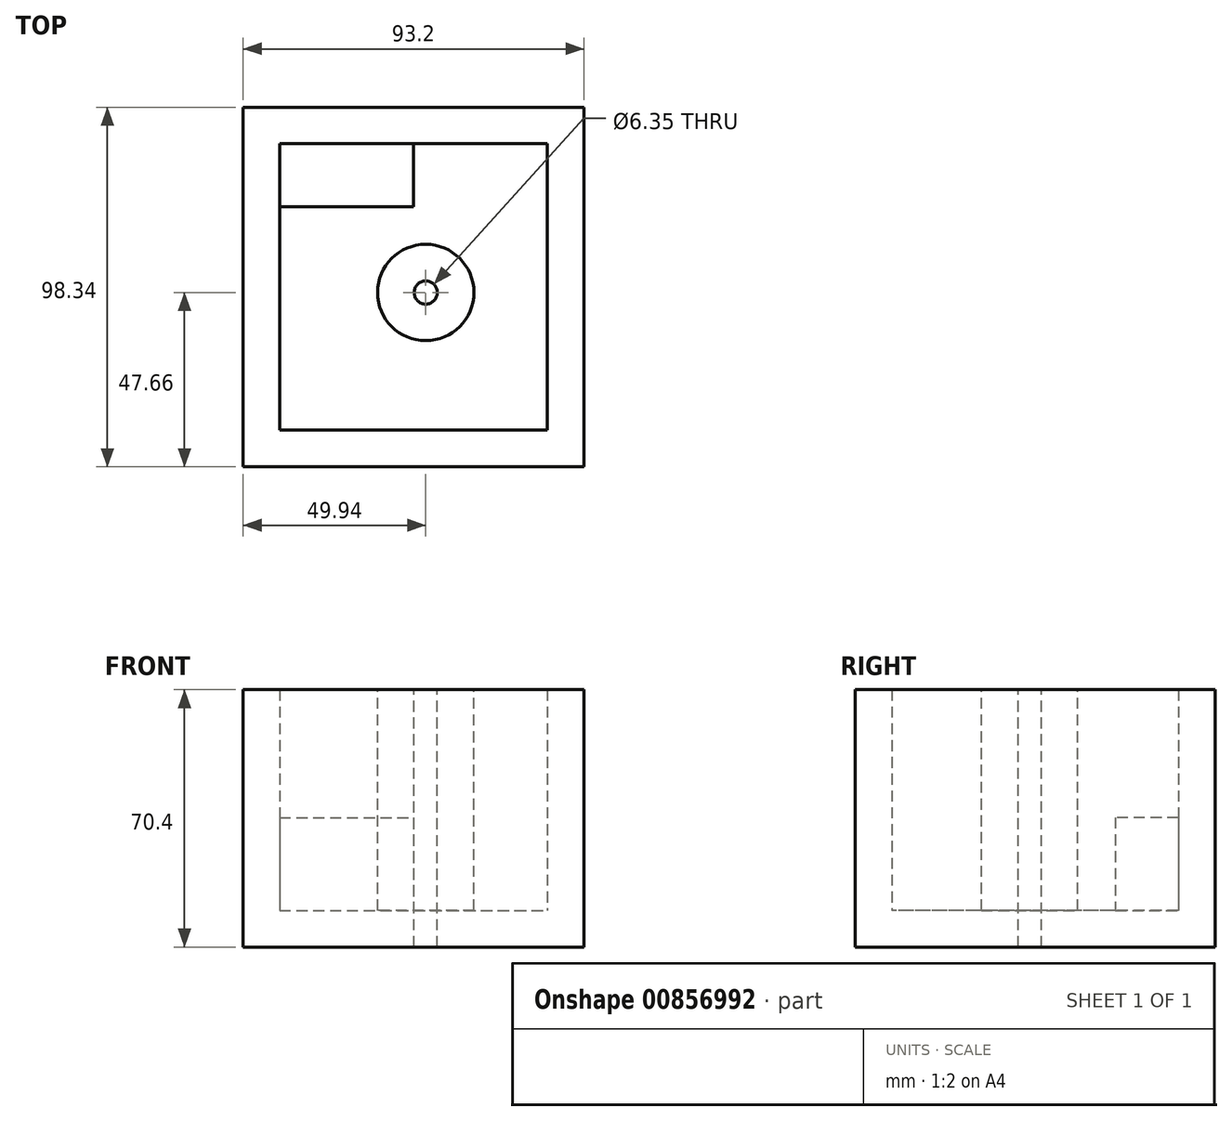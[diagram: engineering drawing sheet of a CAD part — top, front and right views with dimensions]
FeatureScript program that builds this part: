
annotation { "Feature Type Name" : "Feature", "Feature Type Description" : "" }
export const myFeature = defineFeature(function(context is Context, id is Id, definition is map)
    precondition{}
    {
        {
            var Q0;
            Q0=qCreatedBy(makeId("Top.planeOp"),FACE);
            var sketch = newSketch(context, id + "F0", { "sketchPlane" : qUnion([Q0])});
            skLineSegment(sketch, "E0.bottom", {"start": v(-49.94, 50.68) * mm, "end": v(43.26, 50.68) * mm});
            skLineSegment(sketch, "E0.top", {"start": v(-49.94, -47.66) * mm, "end": v(43.26, -47.66) * mm});
            skLineSegment(sketch, "E0.left", {"start": v(-49.94, 50.68) * mm, "end": v(-49.94, -47.66) * mm});
            skLineSegment(sketch, "E0.right", {"start": v(43.26, 50.68) * mm, "end": v(43.26, -47.66) * mm});
            skSolve(sketch);
        }
        {
            var Q0;
            Q0=makeQuery(id+"F0.imprint","IMPRINT",FACE,{"disambiguationData":[TD([[makeQuery(id+"F0.imprint","IMPRINT",EDGE,{"derivedFrom":sQuery(id+"F0.wireOp",EDGE,"E0.bottom")}),-1.0]])]});
            extrude(context, id + "F1", {"entities" : qUnion([Q0]), "depth" : 25.4 * mm, "offsetDistance" : 25.4 * mm});
        }
        {
            var Q0;
            Q0=makeQuery(id+"F1.opExtrude","CAP_FACE",FACE,{"disambiguationData":[OSD([sQuery(id+"F0.wireOp",EDGE,"E0.bottom"),sQuery(id+"F0.wireOp",EDGE,"E0.top"),sQuery(id+"F0.wireOp",EDGE,"E0.left"),sQuery(id+"F0.wireOp",EDGE,"E0.right")])],"isStart":false});
            extrude(context, id + "F2", {"entities" : qUnion([Q0]), "operationType" : NewBodyOperationType.ADD, "depth" : 45 * mm, "offsetDistance" : 25.4 * mm});
        }
        {
            var Q0;
            Q0=makeQuery(id+"F2.opExtrude","CAP_FACE",FACE,{"disambiguationData":[OSD([sQuery(id+"F0.wireOp",EDGE,"E0.bottom"),sQuery(id+"F0.wireOp",EDGE,"E0.top"),sQuery(id+"F0.wireOp",EDGE,"E0.left"),sQuery(id+"F0.wireOp",EDGE,"E0.right")])],"isStart":false});
            var sketch = newSketch(context, id + "F3", { "sketchPlane" : qUnion([Q0])});
            skCircle(sketch, "E1", {"center": v(0, 0) * mm, "radius": 20.07 * mm});
            skSolve(sketch);
        }
        {
            var Q0;
            Q0=sQuery(id+"F3.wireOp",VERTEX,"E1.center");
            var Q1;
            Q1=makeQuery(id+"F1.opExtrude","SWEPT_BODY",BODY,{"disambiguationData":[OSD([sQuery(id+"F0.wireOp",EDGE,"E0.bottom"),sQuery(id+"F0.wireOp",EDGE,"E0.top"),sQuery(id+"F0.wireOp",EDGE,"E0.left"),sQuery(id+"F0.wireOp",EDGE,"E0.right")])]});
            hole(context, id + "F4", {"style" : HoleStyle.SIMPLE, "endStyle" : HoleEndStyle.THROUGH, "holeDiameter" : 6.35 * mm, "majorDiameter" : 6.35 * mm, "isTappedThrough" : true, "tappedDepth" : 12.7 * mm, "tapClearance" : 3, "locations" : qUnion([Q0]), "scope" : qUnion([Q1])});
        }
        {
            var Q0;
            Q0=makeQuery(id+"F2.opExtrude","CAP_FACE",FACE,{"disambiguationData":[OSD([sQuery(id+"F0.wireOp",EDGE,"E0.bottom"),sQuery(id+"F0.wireOp",EDGE,"E0.top"),sQuery(id+"F0.wireOp",EDGE,"E0.left"),sQuery(id+"F0.wireOp",EDGE,"E0.right")])],"isStart":false});
            var sketch = newSketch(context, id + "F5", { "sketchPlane" : qUnion([Q0])});
            skCircle(sketch, "E2", {"center": v(0, 0) * mm, "radius": 11.75 * mm});
            skSolve(sketch);
        }
        {
            var Q0;
            Q0=sQuery(id+"F5.wireOp",EDGE,"E2");
            extrude(context, id + "F6", {"bodyType" : ToolBodyType.SURFACE, "surfaceEntities" : qUnion([Q0]), "oppositeDirection" : true, "depth" : 40 * mm, "offsetDistance" : 25.4 * mm});
        }
        {
            var Q0;
            Q0=makeQuery(id+"F2.opExtrude","CAP_FACE",FACE,{"disambiguationData":[OSD([sQuery(id+"F0.wireOp",EDGE,"E0.bottom"),sQuery(id+"F0.wireOp",EDGE,"E0.top"),sQuery(id+"F0.wireOp",EDGE,"E0.left"),sQuery(id+"F0.wireOp",EDGE,"E0.right")])],"isStart":false});
            shell(context, id + "F7", {"entities" : qUnion([Q0]), "thickness" : 10 * mm});
        }
        {
            var Q0;
            {var subQ0=sQuery(id+"F0.wireOp",EDGE,"E0.right");var subQ1=sQuery(id+"F0.wireOp",EDGE,"E0.left");var subQ2=sQuery(id+"F0.wireOp",EDGE,"E0.top");var subQ3=sQuery(id+"F0.wireOp",EDGE,"E0.bottom");Q0=makeQuery(id+"F7.opShell","OFFSET_FACE",FACE,{"disambiguationData":[OSD([subQ3,subQ2,subQ1,subQ0]),TDD([makeQuery(id+"F1.opExtrude","CAP_FACE",FACE,{"disambiguationData":[OSD([subQ3,subQ2,subQ1,subQ0])],"isStart":true})])]});}
            var sketch = newSketch(context, id + "F8", { "sketchPlane" : qUnion([Q0])});
            skLineSegment(sketch, "E3.bottom", {"start": v(-39.94, 23.46) * mm, "end": v(-3.34, 23.46) * mm});
            skLineSegment(sketch, "E3.top", {"start": v(-39.94, 40.68) * mm, "end": v(-3.34, 40.68) * mm});
            skLineSegment(sketch, "E3.left", {"start": v(-39.94, 23.46) * mm, "end": v(-39.94, 40.68) * mm});
            skLineSegment(sketch, "E3.right", {"start": v(-3.34, 23.46) * mm, "end": v(-3.34, 40.68) * mm});
            skSolve(sketch);
        }
        {
            var Q0;
            Q0 = qSketchRegion(id + "F8", true);
            extrude(context, id + "F9", {"entities" : qUnion([Q0]), "operationType" : NewBodyOperationType.ADD, "depth" : 25.4 * mm, "offsetDistance" : 25.4 * mm});
        }
    });
